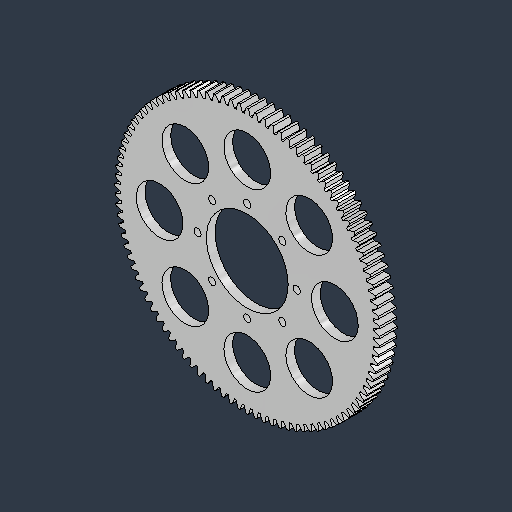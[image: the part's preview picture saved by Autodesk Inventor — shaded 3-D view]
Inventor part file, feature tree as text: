
AUTODESK INVENTOR PART (.ipt)
format: ipt  version: 2024.3 (Build 283343000, 343)  size: 620,544 bytes
history: native  units: mm (DEFAULTED — no unit token found)
features: sketch x5, plane x3, other x3, hole x3, pattern_circular x2, extrude x1, revolve x1, projected_geometry x1
ambient origin geometry x8: Origin, YZ Plane, XZ Plane, XY Plane, X Axis, Y Axis, Z Axis, Center Point
bodies: Solid1 (feature_tree)
feature tree (19):
  extrude  "Extrusion1"  Depth=9.525mm TaperAngle=0.0deg
  plane  "Work Plane1"
  plane  "Work Plane2"
  plane  "Work Plane3"
  other  "Spur Gear"
  hole  "Hole1"  [1 undecoded]
  revolve  "Revolution1"  [1 undecoded]
  hole  "Hole2"  [1 undecoded]
  pattern_circular  "Circular Pattern1"  Angle=135.0deg  [1 undecoded]
  hole  "Hole3"  [1 undecoded]
  pattern_circular  "Circular Pattern2"  [2 undecoded]
  sketch  "Sketch1"  dims[d0=143.928178mm d1=9.525mm d2=0.0mm]
  other  "Srf1"
  sketch  "Sketch3"  dims[d3=141.111111mm d4=76.2mm d5=0.0mm]
  sketch  "Sketch4"  dims[d6=0.0mm d7=0.314159mm d9=0.0mm]
  sketch  "Sketch5"  dims[d14=0.0mm d15=88.441052mm d16=0.0mm]
  sketch  "Sketch6"  dims[d17=0.0mm d18=0.0mm d19=88.441052mm d20=44.45mm d21=19.05mm d22=9.779mm d23=1.9558mm d24=14.3117mm d25=25.4mm d26=20.594885mm d27=135.0deg d28=4.7625mm d30=4.7625mm d31=90.0deg d32=47.625mm d33=25.4mm d34=19.05mm d35=9.525mm d36=6.35mm d37=14.3117mm d38=25.4mm d39=20.594885mm d40=80.0mm d41=360.0deg d43=26.9875mm d44=3.9624mm d45=9.652mm d46=9.525mm d47=6.35mm d48=14.3117mm d49=25.4mm d50=20.594885mm d51=80.0mm d52=360.0deg]
  other  "Pitch Diameter"
  projected_geometry  "Project Cut Edges1"
note: 7 required parameter values undecoded (feature->parameter linkage not recoverable at this tier; creation-order binding heuristic only, values carry confidence <= 0.55)